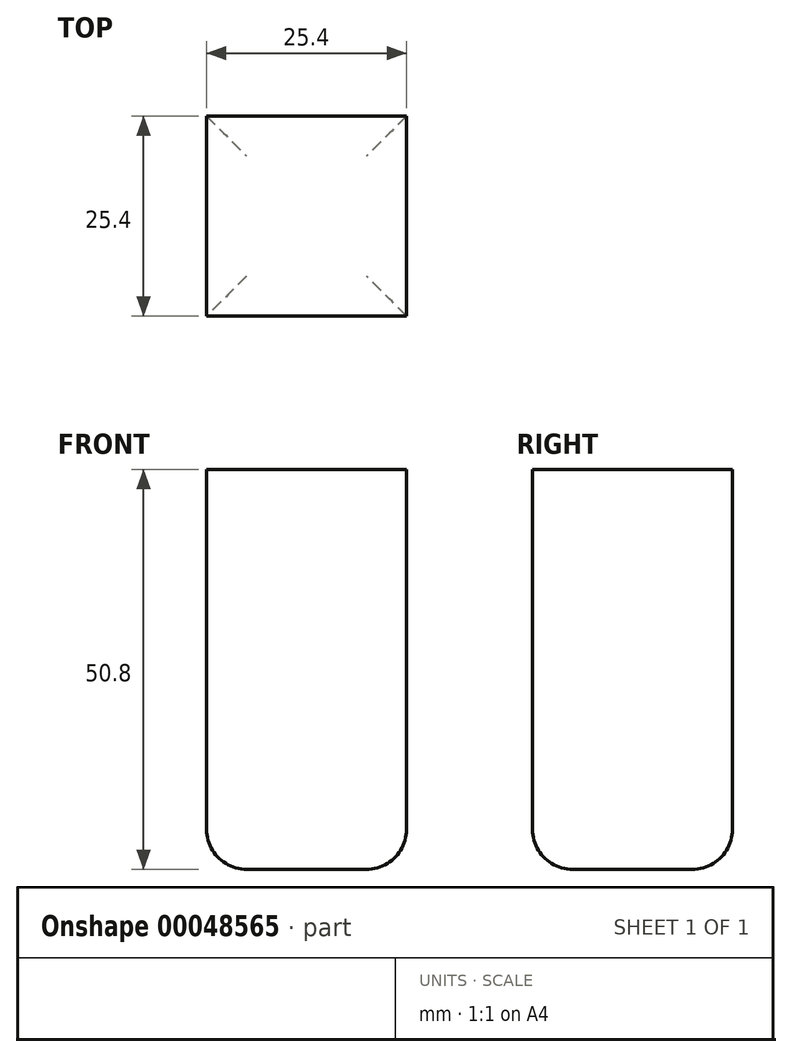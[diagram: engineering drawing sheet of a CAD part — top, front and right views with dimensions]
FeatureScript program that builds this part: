
annotation { "Feature Type Name" : "Feature", "Feature Type Description" : "" }
export const myFeature = defineFeature(function(context is Context, id is Id, definition is map)
    precondition{}
    {
        {
            var Q0;
            Q0=qCreatedBy(makeId("Front.planeOp"),FACE);
            var sketch = newSketch(context, id + "F0", { "sketchPlane" : qUnion([Q0])});
            skLineSegment(sketch, "E0.rect.bottom", {"start": v(-12.7, -25.4) * mm, "end": v(12.7, -25.4) * mm});
            skLineSegment(sketch, "E0.rect.top", {"start": v(-12.7, 25.4) * mm, "end": v(12.7, 25.4) * mm});
            skLineSegment(sketch, "E0.rect.left", {"start": v(-12.7, -25.4) * mm, "end": v(-12.7, 25.4) * mm});
            skLineSegment(sketch, "E0.rect.right", {"start": v(12.7, -25.4) * mm, "end": v(12.7, 25.4) * mm});
            skPoint(sketch, "E0.rect.middle", {"position": v(0, 0) * mm});
            skSolve(sketch);
        }
        {
            var Q0;
            Q0 = qSketchRegion(id + "F0", true);
            extrude(context, id + "F1", {"entities" : qUnion([Q0]), "depth" : 25.4 * mm});
        }
        {
            var Q0;
            Q0=makeQuery(id+"F1.opExtrude","SWEPT_EDGE",EDGE,{"disambiguationData":[OSD([sQuery(id+"F0.wireOp",EDGE,"E0.rect.bottom"),sQuery(id+"F0.wireOp",EDGE,"E0.rect.right")])]});
            var Q1;
            Q1=makeQuery(id+"F1.opExtrude","CAP_EDGE",EDGE,{"disambiguationData":[OSD([sQuery(id+"F0.wireOp",EDGE,"E0.rect.bottom")])],"isStart":false});
            var Q2;
            Q2=makeQuery(id+"F1.opExtrude","SWEPT_EDGE",EDGE,{"disambiguationData":[OSD([sQuery(id+"F0.wireOp",EDGE,"E0.rect.bottom"),sQuery(id+"F0.wireOp",EDGE,"E0.rect.left")])]});
            var Q3;
            Q3=makeQuery(id+"F1.opExtrude","CAP_EDGE",EDGE,{"disambiguationData":[OSD([sQuery(id+"F0.wireOp",EDGE,"E0.rect.bottom")])],"isStart":true});
            fillet(context, id + "F2", {"entities" : qUnion([Q0, Q1, Q2, Q3]), "radius" : 5.08 * mm, "tangentPropagation" : true, "allowEdgeOverflow" : false});
        }
    });
